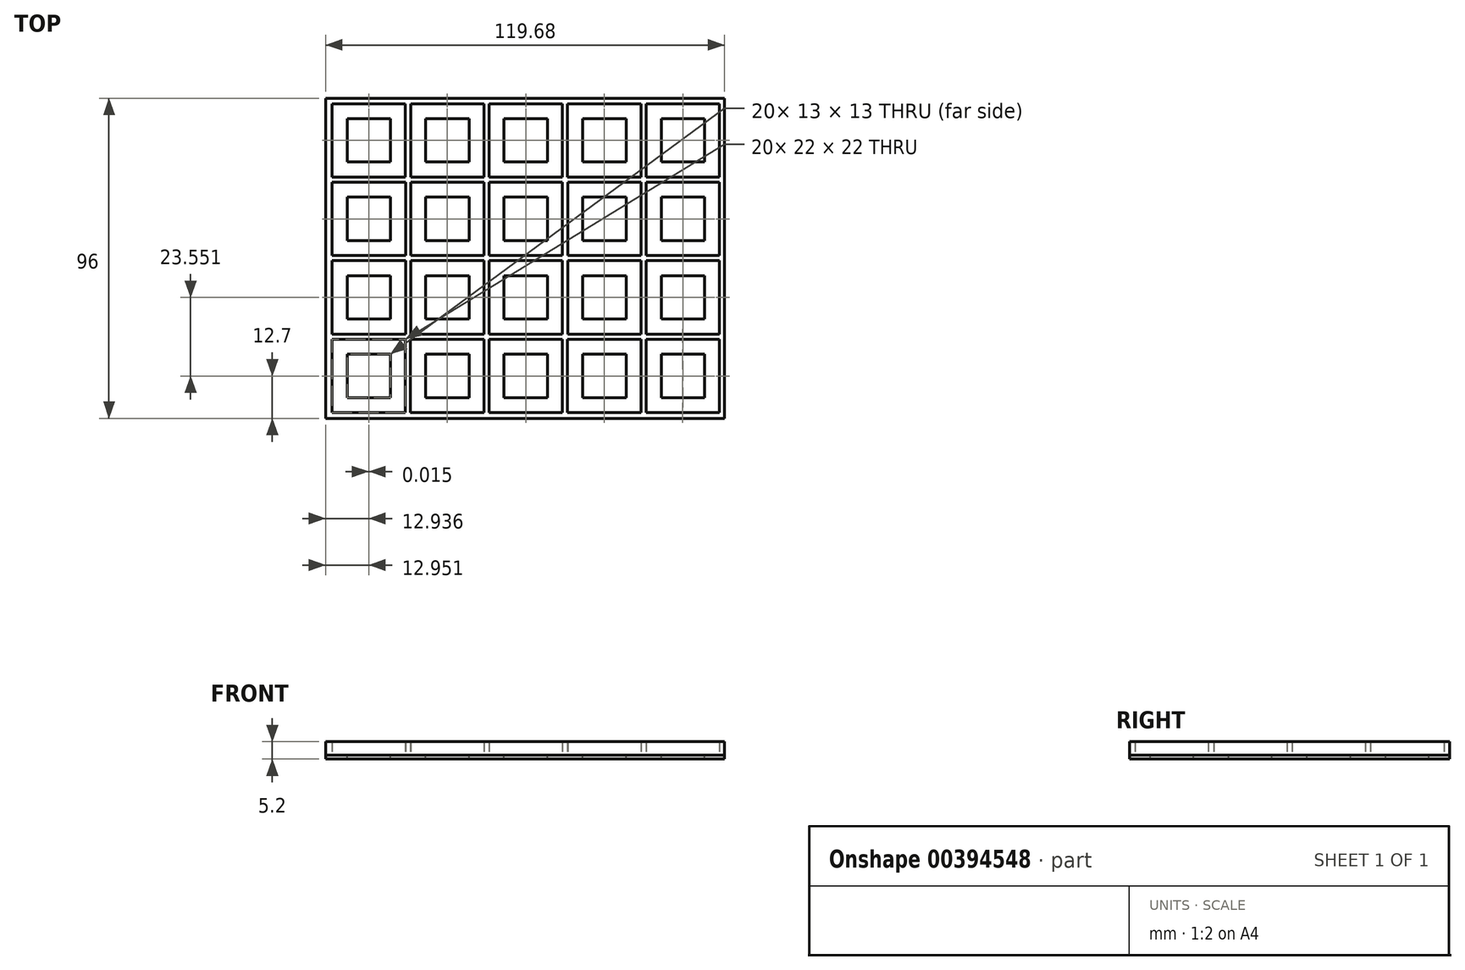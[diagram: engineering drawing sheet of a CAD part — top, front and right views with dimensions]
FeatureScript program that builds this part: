
annotation { "Feature Type Name" : "Feature", "Feature Type Description" : "" }
export const myFeature = defineFeature(function(context is Context, id is Id, definition is map)
    precondition{}
    {
        {
            var Q0;
            Q0=qCreatedBy(makeId("Top.planeOp"),FACE);
            var sketch = newSketch(context, id + "F0", { "sketchPlane" : qUnion([Q0])});
            skLineSegment(sketch, "E0", {"start": v(59.84, -48) * mm, "end": v(-59.84, -48) * mm});
            skLineSegment(sketch, "E1", {"start": v(-59.84, -48) * mm, "end": v(-59.84, 48) * mm});
            skLineSegment(sketch, "E2", {"start": v(-59.84, 48) * mm, "end": v(59.84, 48) * mm});
            skLineSegment(sketch, "E3", {"start": v(59.84, 48) * mm, "end": v(59.84, -48) * mm});
            skLineSegment(sketch, "E4", {"start": v(-35.89, 24.35) * mm, "end": v(-57.89, 24.35) * mm});
            skLineSegment(sketch, "E5", {"start": v(-57.89, 24.35) * mm, "end": v(-57.89, 46.35) * mm});
            skLineSegment(sketch, "E6", {"start": v(-57.89, 46.35) * mm, "end": v(-35.89, 46.35) * mm});
            skLineSegment(sketch, "E7", {"start": v(-35.89, 46.35) * mm, "end": v(-35.89, 24.35) * mm});
            skLineSegment(sketch, "E8", {"start": v(-35.86, 0.8) * mm, "end": v(-57.86, 0.8) * mm});
            skLineSegment(sketch, "E9", {"start": v(-57.86, 0.8) * mm, "end": v(-57.86, 22.8) * mm});
            skLineSegment(sketch, "E10", {"start": v(-57.86, 22.8) * mm, "end": v(-35.86, 22.8) * mm});
            skLineSegment(sketch, "E11", {"start": v(-35.86, 22.8) * mm, "end": v(-35.86, 0.8) * mm});
            skLineSegment(sketch, "E12", {"start": v(-35.87, -22.75) * mm, "end": v(-57.87, -22.75) * mm});
            skLineSegment(sketch, "E13", {"start": v(-57.87, -22.75) * mm, "end": v(-57.87, -0.75) * mm});
            skLineSegment(sketch, "E14", {"start": v(-57.87, -0.75) * mm, "end": v(-35.87, -0.75) * mm});
            skLineSegment(sketch, "E15", {"start": v(-35.87, -0.75) * mm, "end": v(-35.87, -22.75) * mm});
            skLineSegment(sketch, "E16", {"start": v(-35.9, -46.3) * mm, "end": v(-57.9, -46.3) * mm});
            skLineSegment(sketch, "E17", {"start": v(-57.9, -46.3) * mm, "end": v(-57.9, -24.3) * mm});
            skLineSegment(sketch, "E18", {"start": v(-57.9, -24.3) * mm, "end": v(-35.9, -24.3) * mm});
            skLineSegment(sketch, "E19", {"start": v(-35.9, -24.3) * mm, "end": v(-35.9, -46.3) * mm});
            skLineSegment(sketch, "E20", {"start": v(-12.34, 24.35) * mm, "end": v(-34.34, 24.35) * mm});
            skLineSegment(sketch, "E21", {"start": v(-34.34, 24.35) * mm, "end": v(-34.34, 46.35) * mm});
            skLineSegment(sketch, "E22", {"start": v(-34.34, 46.35) * mm, "end": v(-12.34, 46.35) * mm});
            skLineSegment(sketch, "E23", {"start": v(-12.34, 46.35) * mm, "end": v(-12.34, 24.35) * mm});
            skLineSegment(sketch, "E24", {"start": v(-12.3, 0.8) * mm, "end": v(-34.3, 0.8) * mm});
            skLineSegment(sketch, "E25", {"start": v(-34.3, 0.8) * mm, "end": v(-34.3, 22.8) * mm});
            skLineSegment(sketch, "E26", {"start": v(-34.3, 22.8) * mm, "end": v(-12.3, 22.8) * mm});
            skLineSegment(sketch, "E27", {"start": v(-12.3, 22.8) * mm, "end": v(-12.3, 0.8) * mm});
            skLineSegment(sketch, "E28", {"start": v(-12.32, -22.75) * mm, "end": v(-34.32, -22.75) * mm});
            skLineSegment(sketch, "E29", {"start": v(-34.32, -22.75) * mm, "end": v(-34.32, -0.75) * mm});
            skLineSegment(sketch, "E30", {"start": v(-34.32, -0.75) * mm, "end": v(-12.32, -0.75) * mm});
            skLineSegment(sketch, "E31", {"start": v(-12.32, -0.75) * mm, "end": v(-12.32, -22.75) * mm});
            skLineSegment(sketch, "E32", {"start": v(-12.35, -46.3) * mm, "end": v(-34.35, -46.3) * mm});
            skLineSegment(sketch, "E33", {"start": v(-34.35, -46.3) * mm, "end": v(-34.35, -24.3) * mm});
            skLineSegment(sketch, "E34", {"start": v(-34.35, -24.3) * mm, "end": v(-12.35, -24.3) * mm});
            skLineSegment(sketch, "E35", {"start": v(-12.35, -24.3) * mm, "end": v(-12.35, -46.3) * mm});
            skLineSegment(sketch, "E36", {"start": v(11.21, 24.35) * mm, "end": v(-10.79, 24.35) * mm});
            skLineSegment(sketch, "E37", {"start": v(-10.79, 24.35) * mm, "end": v(-10.79, 46.35) * mm});
            skLineSegment(sketch, "E38", {"start": v(-10.79, 46.35) * mm, "end": v(11.21, 46.35) * mm});
            skLineSegment(sketch, "E39", {"start": v(11.21, 46.35) * mm, "end": v(11.21, 24.35) * mm});
            skLineSegment(sketch, "E40", {"start": v(11.24, 0.8) * mm, "end": v(-10.76, 0.8) * mm});
            skLineSegment(sketch, "E41", {"start": v(-10.76, 0.8) * mm, "end": v(-10.76, 22.8) * mm});
            skLineSegment(sketch, "E42", {"start": v(-10.76, 22.8) * mm, "end": v(11.24, 22.8) * mm});
            skLineSegment(sketch, "E43", {"start": v(11.24, 22.8) * mm, "end": v(11.24, 0.8) * mm});
            skLineSegment(sketch, "E44", {"start": v(11.23, -22.75) * mm, "end": v(-10.77, -22.75) * mm});
            skLineSegment(sketch, "E45", {"start": v(-10.77, -22.75) * mm, "end": v(-10.77, -0.75) * mm});
            skLineSegment(sketch, "E46", {"start": v(-10.77, -0.75) * mm, "end": v(11.23, -0.75) * mm});
            skLineSegment(sketch, "E47", {"start": v(11.23, -0.75) * mm, "end": v(11.23, -22.75) * mm});
            skLineSegment(sketch, "E48", {"start": v(11.2, -46.3) * mm, "end": v(-10.8, -46.3) * mm});
            skLineSegment(sketch, "E49", {"start": v(-10.8, -46.3) * mm, "end": v(-10.8, -24.3) * mm});
            skLineSegment(sketch, "E50", {"start": v(-10.8, -24.3) * mm, "end": v(11.2, -24.3) * mm});
            skLineSegment(sketch, "E51", {"start": v(11.2, -24.3) * mm, "end": v(11.2, -46.3) * mm});
            skLineSegment(sketch, "E52", {"start": v(34.76, 24.35) * mm, "end": v(12.76, 24.35) * mm});
            skLineSegment(sketch, "E53", {"start": v(12.76, 24.35) * mm, "end": v(12.76, 46.35) * mm});
            skLineSegment(sketch, "E54", {"start": v(12.76, 46.35) * mm, "end": v(34.76, 46.35) * mm});
            skLineSegment(sketch, "E55", {"start": v(34.76, 46.35) * mm, "end": v(34.76, 24.35) * mm});
            skLineSegment(sketch, "E56", {"start": v(34.8, 0.8) * mm, "end": v(12.8, 0.8) * mm});
            skLineSegment(sketch, "E57", {"start": v(12.8, 0.8) * mm, "end": v(12.8, 22.8) * mm});
            skLineSegment(sketch, "E58", {"start": v(12.8, 22.8) * mm, "end": v(34.8, 22.8) * mm});
            skLineSegment(sketch, "E59", {"start": v(34.8, 22.8) * mm, "end": v(34.8, 0.8) * mm});
            skLineSegment(sketch, "E60", {"start": v(34.78, -22.75) * mm, "end": v(12.78, -22.75) * mm});
            skLineSegment(sketch, "E61", {"start": v(12.78, -22.75) * mm, "end": v(12.78, -0.75) * mm});
            skLineSegment(sketch, "E62", {"start": v(12.78, -0.75) * mm, "end": v(34.78, -0.75) * mm});
            skLineSegment(sketch, "E63", {"start": v(34.78, -0.75) * mm, "end": v(34.78, -22.75) * mm});
            skLineSegment(sketch, "E64", {"start": v(34.75, -46.3) * mm, "end": v(12.75, -46.3) * mm});
            skLineSegment(sketch, "E65", {"start": v(12.75, -46.3) * mm, "end": v(12.75, -24.3) * mm});
            skLineSegment(sketch, "E66", {"start": v(12.75, -24.3) * mm, "end": v(34.75, -24.3) * mm});
            skLineSegment(sketch, "E67", {"start": v(34.75, -24.3) * mm, "end": v(34.75, -46.3) * mm});
            skLineSegment(sketch, "E68", {"start": v(58.31, 24.35) * mm, "end": v(36.31, 24.35) * mm});
            skLineSegment(sketch, "E69", {"start": v(36.31, 24.35) * mm, "end": v(36.31, 46.35) * mm});
            skLineSegment(sketch, "E70", {"start": v(36.31, 46.35) * mm, "end": v(58.31, 46.35) * mm});
            skLineSegment(sketch, "E71", {"start": v(58.31, 46.35) * mm, "end": v(58.31, 24.35) * mm});
            skLineSegment(sketch, "E72", {"start": v(58.34, 0.8) * mm, "end": v(36.34, 0.8) * mm});
            skLineSegment(sketch, "E73", {"start": v(36.34, 0.8) * mm, "end": v(36.34, 22.8) * mm});
            skLineSegment(sketch, "E74", {"start": v(36.34, 22.8) * mm, "end": v(58.34, 22.8) * mm});
            skLineSegment(sketch, "E75", {"start": v(58.34, 22.8) * mm, "end": v(58.34, 0.8) * mm});
            skLineSegment(sketch, "E76", {"start": v(58.33, -22.75) * mm, "end": v(36.33, -22.75) * mm});
            skLineSegment(sketch, "E77", {"start": v(36.33, -22.75) * mm, "end": v(36.33, -0.75) * mm});
            skLineSegment(sketch, "E78", {"start": v(36.33, -0.75) * mm, "end": v(58.33, -0.75) * mm});
            skLineSegment(sketch, "E79", {"start": v(58.33, -0.75) * mm, "end": v(58.33, -22.75) * mm});
            skLineSegment(sketch, "E80", {"start": v(58.3, -46.3) * mm, "end": v(36.3, -46.3) * mm});
            skLineSegment(sketch, "E81", {"start": v(36.3, -46.3) * mm, "end": v(36.3, -24.3) * mm});
            skLineSegment(sketch, "E82", {"start": v(36.3, -24.3) * mm, "end": v(58.3, -24.3) * mm});
            skLineSegment(sketch, "E83", {"start": v(58.3, -24.3) * mm, "end": v(58.3, -46.3) * mm});
            skLineSegment(sketch, "E84", {"start": v(-40.39, 28.85) * mm, "end": v(-53.39, 28.85) * mm});
            skLineSegment(sketch, "E85", {"start": v(-53.39, 28.85) * mm, "end": v(-53.39, 41.85) * mm});
            skLineSegment(sketch, "E86", {"start": v(-53.39, 41.85) * mm, "end": v(-40.39, 41.85) * mm});
            skLineSegment(sketch, "E87", {"start": v(-40.39, 41.85) * mm, "end": v(-40.39, 28.85) * mm});
            skLineSegment(sketch, "E88", {"start": v(-16.8, 28.85) * mm, "end": v(-29.8, 28.85) * mm});
            skLineSegment(sketch, "E89", {"start": v(-29.8, 28.85) * mm, "end": v(-29.8, 41.85) * mm});
            skLineSegment(sketch, "E90", {"start": v(-29.8, 41.85) * mm, "end": v(-16.8, 41.85) * mm});
            skLineSegment(sketch, "E91", {"start": v(-16.8, 41.85) * mm, "end": v(-16.8, 28.85) * mm});
            skLineSegment(sketch, "E92", {"start": v(6.7, 28.85) * mm, "end": v(-6.3, 28.85) * mm});
            skLineSegment(sketch, "E93", {"start": v(-6.3, 28.85) * mm, "end": v(-6.3, 41.85) * mm});
            skLineSegment(sketch, "E94", {"start": v(-6.3, 41.85) * mm, "end": v(6.7, 41.85) * mm});
            skLineSegment(sketch, "E95", {"start": v(6.7, 41.85) * mm, "end": v(6.7, 28.85) * mm});
            skLineSegment(sketch, "E96", {"start": v(30.3, 28.85) * mm, "end": v(17.3, 28.85) * mm});
            skLineSegment(sketch, "E97", {"start": v(17.3, 28.85) * mm, "end": v(17.3, 41.85) * mm});
            skLineSegment(sketch, "E98", {"start": v(17.3, 41.85) * mm, "end": v(30.3, 41.85) * mm});
            skLineSegment(sketch, "E99", {"start": v(30.3, 41.85) * mm, "end": v(30.3, 28.85) * mm});
            skLineSegment(sketch, "E100", {"start": v(53.84, 28.85) * mm, "end": v(40.84, 28.85) * mm});
            skLineSegment(sketch, "E101", {"start": v(40.84, 28.85) * mm, "end": v(40.84, 41.85) * mm});
            skLineSegment(sketch, "E102", {"start": v(40.84, 41.85) * mm, "end": v(53.84, 41.85) * mm});
            skLineSegment(sketch, "E103", {"start": v(53.84, 41.85) * mm, "end": v(53.84, 28.85) * mm});
            skLineSegment(sketch, "E104", {"start": v(-40.39, 5.3) * mm, "end": v(-53.39, 5.3) * mm});
            skLineSegment(sketch, "E105", {"start": v(-53.39, 5.3) * mm, "end": v(-53.39, 18.3) * mm});
            skLineSegment(sketch, "E106", {"start": v(-53.39, 18.3) * mm, "end": v(-40.39, 18.3) * mm});
            skLineSegment(sketch, "E107", {"start": v(-40.39, 18.3) * mm, "end": v(-40.39, 5.3) * mm});
            skLineSegment(sketch, "E108", {"start": v(-16.8, 5.3) * mm, "end": v(-29.8, 5.3) * mm});
            skLineSegment(sketch, "E109", {"start": v(-29.8, 5.3) * mm, "end": v(-29.8, 18.3) * mm});
            skLineSegment(sketch, "E110", {"start": v(-29.8, 18.3) * mm, "end": v(-16.8, 18.3) * mm});
            skLineSegment(sketch, "E111", {"start": v(-16.8, 18.3) * mm, "end": v(-16.8, 5.3) * mm});
            skLineSegment(sketch, "E112", {"start": v(6.7, 5.3) * mm, "end": v(-6.3, 5.3) * mm});
            skLineSegment(sketch, "E113", {"start": v(-6.3, 5.3) * mm, "end": v(-6.3, 18.3) * mm});
            skLineSegment(sketch, "E114", {"start": v(-6.3, 18.3) * mm, "end": v(6.7, 18.3) * mm});
            skLineSegment(sketch, "E115", {"start": v(6.7, 18.3) * mm, "end": v(6.7, 5.3) * mm});
            skLineSegment(sketch, "E116", {"start": v(30.3, 5.3) * mm, "end": v(17.3, 5.3) * mm});
            skLineSegment(sketch, "E117", {"start": v(17.3, 5.3) * mm, "end": v(17.3, 18.3) * mm});
            skLineSegment(sketch, "E118", {"start": v(17.3, 18.3) * mm, "end": v(30.3, 18.3) * mm});
            skLineSegment(sketch, "E119", {"start": v(30.3, 18.3) * mm, "end": v(30.3, 5.3) * mm});
            skLineSegment(sketch, "E120", {"start": v(53.84, 5.3) * mm, "end": v(40.84, 5.3) * mm});
            skLineSegment(sketch, "E121", {"start": v(40.84, 5.3) * mm, "end": v(40.84, 18.3) * mm});
            skLineSegment(sketch, "E122", {"start": v(40.84, 18.3) * mm, "end": v(53.84, 18.3) * mm});
            skLineSegment(sketch, "E123", {"start": v(53.84, 18.3) * mm, "end": v(53.84, 5.3) * mm});
            skLineSegment(sketch, "E124", {"start": v(-40.39, -18.25) * mm, "end": v(-53.39, -18.25) * mm});
            skLineSegment(sketch, "E125", {"start": v(-53.39, -18.25) * mm, "end": v(-53.39, -5.25) * mm});
            skLineSegment(sketch, "E126", {"start": v(-53.39, -5.25) * mm, "end": v(-40.39, -5.25) * mm});
            skLineSegment(sketch, "E127", {"start": v(-40.39, -5.25) * mm, "end": v(-40.39, -18.25) * mm});
            skLineSegment(sketch, "E128", {"start": v(-16.8, -18.25) * mm, "end": v(-29.8, -18.25) * mm});
            skLineSegment(sketch, "E129", {"start": v(-29.8, -18.25) * mm, "end": v(-29.8, -5.25) * mm});
            skLineSegment(sketch, "E130", {"start": v(-29.8, -5.25) * mm, "end": v(-16.8, -5.25) * mm});
            skLineSegment(sketch, "E131", {"start": v(-16.8, -5.25) * mm, "end": v(-16.8, -18.25) * mm});
            skLineSegment(sketch, "E132", {"start": v(6.7, -18.25) * mm, "end": v(-6.3, -18.25) * mm});
            skLineSegment(sketch, "E133", {"start": v(-6.3, -18.25) * mm, "end": v(-6.3, -5.25) * mm});
            skLineSegment(sketch, "E134", {"start": v(-6.3, -5.25) * mm, "end": v(6.7, -5.25) * mm});
            skLineSegment(sketch, "E135", {"start": v(6.7, -5.25) * mm, "end": v(6.7, -18.25) * mm});
            skLineSegment(sketch, "E136", {"start": v(30.3, -18.25) * mm, "end": v(17.3, -18.25) * mm});
            skLineSegment(sketch, "E137", {"start": v(17.3, -18.25) * mm, "end": v(17.3, -5.25) * mm});
            skLineSegment(sketch, "E138", {"start": v(17.3, -5.25) * mm, "end": v(30.3, -5.25) * mm});
            skLineSegment(sketch, "E139", {"start": v(30.3, -5.25) * mm, "end": v(30.3, -18.25) * mm});
            skLineSegment(sketch, "E140", {"start": v(53.84, -18.25) * mm, "end": v(40.84, -18.25) * mm});
            skLineSegment(sketch, "E141", {"start": v(40.84, -18.25) * mm, "end": v(40.84, -5.25) * mm});
            skLineSegment(sketch, "E142", {"start": v(40.84, -5.25) * mm, "end": v(53.84, -5.25) * mm});
            skLineSegment(sketch, "E143", {"start": v(53.84, -5.25) * mm, "end": v(53.84, -18.25) * mm});
            skLineSegment(sketch, "E144", {"start": v(-40.39, -41.8) * mm, "end": v(-53.39, -41.8) * mm});
            skLineSegment(sketch, "E145", {"start": v(-53.39, -41.8) * mm, "end": v(-53.39, -28.8) * mm});
            skLineSegment(sketch, "E146", {"start": v(-53.39, -28.8) * mm, "end": v(-40.39, -28.8) * mm});
            skLineSegment(sketch, "E147", {"start": v(-40.39, -28.8) * mm, "end": v(-40.39, -41.8) * mm});
            skLineSegment(sketch, "E148", {"start": v(-16.8, -41.8) * mm, "end": v(-29.8, -41.8) * mm});
            skLineSegment(sketch, "E149", {"start": v(-29.8, -41.8) * mm, "end": v(-29.8, -28.8) * mm});
            skLineSegment(sketch, "E150", {"start": v(-29.8, -28.8) * mm, "end": v(-16.8, -28.8) * mm});
            skLineSegment(sketch, "E151", {"start": v(-16.8, -28.8) * mm, "end": v(-16.8, -41.8) * mm});
            skLineSegment(sketch, "E152", {"start": v(6.7, -41.8) * mm, "end": v(-6.3, -41.8) * mm});
            skLineSegment(sketch, "E153", {"start": v(-6.3, -41.8) * mm, "end": v(-6.3, -28.8) * mm});
            skLineSegment(sketch, "E154", {"start": v(-6.3, -28.8) * mm, "end": v(6.7, -28.8) * mm});
            skLineSegment(sketch, "E155", {"start": v(6.7, -28.8) * mm, "end": v(6.7, -41.8) * mm});
            skLineSegment(sketch, "E156", {"start": v(30.3, -41.8) * mm, "end": v(17.3, -41.8) * mm});
            skLineSegment(sketch, "E157", {"start": v(17.3, -41.8) * mm, "end": v(17.3, -28.8) * mm});
            skLineSegment(sketch, "E158", {"start": v(17.3, -28.8) * mm, "end": v(30.3, -28.8) * mm});
            skLineSegment(sketch, "E159", {"start": v(30.3, -28.8) * mm, "end": v(30.3, -41.8) * mm});
            skLineSegment(sketch, "E160", {"start": v(53.84, -41.8) * mm, "end": v(40.84, -41.8) * mm});
            skLineSegment(sketch, "E161", {"start": v(40.84, -41.8) * mm, "end": v(40.84, -28.8) * mm});
            skLineSegment(sketch, "E162", {"start": v(40.84, -28.8) * mm, "end": v(53.84, -28.8) * mm});
            skLineSegment(sketch, "E163", {"start": v(53.84, -28.8) * mm, "end": v(53.84, -41.8) * mm});
            skSolve(sketch);
        }
        {
            var Q0;
            Q0=makeQuery(id+"F0.imprint","IMPRINT",FACE,{"disambiguationData":[TD([[makeQuery(id+"F0.imprint","IMPRINT",EDGE,{"derivedFrom":sQuery(id+"F0.wireOp",EDGE,"E0")}),-1.0]])]});
            extrude(context, id + "F1", {"entities" : qUnion([Q0]), "depth" : 4 * mm});
        }
        {
            var Q0;
            Q0=makeQuery(id+"F0.imprint","IMPRINT",FACE,{"disambiguationData":[TD([[makeQuery(id+"F0.imprint","IMPRINT",EDGE,{"derivedFrom":sQuery(id+"F0.wireOp",EDGE,"E64")}),-1.0]])]});
            var Q1;
            Q1=makeQuery(id+"F0.imprint","IMPRINT",FACE,{"disambiguationData":[TD([[makeQuery(id+"F0.imprint","IMPRINT",EDGE,{"derivedFrom":sQuery(id+"F0.wireOp",EDGE,"E28")}),-1.0]])]});
            var Q2;
            Q2=makeQuery(id+"F0.imprint","IMPRINT",FACE,{"disambiguationData":[TD([[makeQuery(id+"F0.imprint","IMPRINT",EDGE,{"derivedFrom":sQuery(id+"F0.wireOp",EDGE,"E4")}),-1.0]])]});
            var Q3;
            Q3=makeQuery(id+"F0.imprint","IMPRINT",FACE,{"disambiguationData":[TD([[makeQuery(id+"F0.imprint","IMPRINT",EDGE,{"derivedFrom":sQuery(id+"F0.wireOp",EDGE,"E68")}),-1.0]])]});
            var Q4;
            Q4=makeQuery(id+"F0.imprint","IMPRINT",FACE,{"disambiguationData":[TD([[makeQuery(id+"F0.imprint","IMPRINT",EDGE,{"derivedFrom":sQuery(id+"F0.wireOp",EDGE,"E40")}),-1.0]])]});
            var Q5;
            Q5=makeQuery(id+"F0.imprint","IMPRINT",FACE,{"disambiguationData":[TD([[makeQuery(id+"F0.imprint","IMPRINT",EDGE,{"derivedFrom":sQuery(id+"F0.wireOp",EDGE,"E32")}),-1.0]])]});
            var Q6;
            Q6=makeQuery(id+"F0.imprint","IMPRINT",FACE,{"disambiguationData":[TD([[makeQuery(id+"F0.imprint","IMPRINT",EDGE,{"derivedFrom":sQuery(id+"F0.wireOp",EDGE,"E8")}),-1.0]])]});
            var Q7;
            Q7=makeQuery(id+"F0.imprint","IMPRINT",FACE,{"disambiguationData":[TD([[makeQuery(id+"F0.imprint","IMPRINT",EDGE,{"derivedFrom":sQuery(id+"F0.wireOp",EDGE,"E44")}),-1.0]])]});
            var Q8;
            Q8=makeQuery(id+"F0.imprint","IMPRINT",FACE,{"disambiguationData":[TD([[makeQuery(id+"F0.imprint","IMPRINT",EDGE,{"derivedFrom":sQuery(id+"F0.wireOp",EDGE,"E72")}),-1.0]])]});
            var Q9;
            Q9=makeQuery(id+"F0.imprint","IMPRINT",FACE,{"disambiguationData":[TD([[makeQuery(id+"F0.imprint","IMPRINT",EDGE,{"derivedFrom":sQuery(id+"F0.wireOp",EDGE,"E36")}),-1.0]])]});
            var Q10;
            Q10=makeQuery(id+"F0.imprint","IMPRINT",FACE,{"disambiguationData":[TD([[makeQuery(id+"F0.imprint","IMPRINT",EDGE,{"derivedFrom":sQuery(id+"F0.wireOp",EDGE,"E76")}),-1.0]])]});
            var Q11;
            Q11=makeQuery(id+"F0.imprint","IMPRINT",FACE,{"disambiguationData":[TD([[makeQuery(id+"F0.imprint","IMPRINT",EDGE,{"derivedFrom":sQuery(id+"F0.wireOp",EDGE,"E12")}),-1.0]])]});
            var Q12;
            Q12=makeQuery(id+"F0.imprint","IMPRINT",FACE,{"disambiguationData":[TD([[makeQuery(id+"F0.imprint","IMPRINT",EDGE,{"derivedFrom":sQuery(id+"F0.wireOp",EDGE,"E52")}),-1.0]])]});
            var Q13;
            Q13=makeQuery(id+"F0.imprint","IMPRINT",FACE,{"disambiguationData":[TD([[makeQuery(id+"F0.imprint","IMPRINT",EDGE,{"derivedFrom":sQuery(id+"F0.wireOp",EDGE,"E80")}),-1.0]])]});
            var Q14;
            Q14=makeQuery(id+"F0.imprint","IMPRINT",FACE,{"disambiguationData":[TD([[makeQuery(id+"F0.imprint","IMPRINT",EDGE,{"derivedFrom":sQuery(id+"F0.wireOp",EDGE,"E16")}),-1.0]])]});
            var Q15;
            Q15=makeQuery(id+"F0.imprint","IMPRINT",FACE,{"disambiguationData":[TD([[makeQuery(id+"F0.imprint","IMPRINT",EDGE,{"derivedFrom":sQuery(id+"F0.wireOp",EDGE,"E56")}),-1.0]])]});
            var Q16;
            Q16=makeQuery(id+"F0.imprint","IMPRINT",FACE,{"disambiguationData":[TD([[makeQuery(id+"F0.imprint","IMPRINT",EDGE,{"derivedFrom":sQuery(id+"F0.wireOp",EDGE,"E0")}),-1.0]])]});
            var Q17;
            Q17=makeQuery(id+"F0.imprint","IMPRINT",FACE,{"disambiguationData":[TD([[makeQuery(id+"F0.imprint","IMPRINT",EDGE,{"derivedFrom":sQuery(id+"F0.wireOp",EDGE,"E20")}),-1.0]])]});
            var Q18;
            Q18=makeQuery(id+"F0.imprint","IMPRINT",FACE,{"disambiguationData":[TD([[makeQuery(id+"F0.imprint","IMPRINT",EDGE,{"derivedFrom":sQuery(id+"F0.wireOp",EDGE,"E60")}),-1.0]])]});
            var Q19;
            Q19=makeQuery(id+"F0.imprint","IMPRINT",FACE,{"disambiguationData":[TD([[makeQuery(id+"F0.imprint","IMPRINT",EDGE,{"derivedFrom":sQuery(id+"F0.wireOp",EDGE,"E48")}),-1.0]])]});
            var Q20;
            Q20=makeQuery(id+"F0.imprint","IMPRINT",FACE,{"disambiguationData":[TD([[makeQuery(id+"F0.imprint","IMPRINT",EDGE,{"derivedFrom":sQuery(id+"F0.wireOp",EDGE,"E24")}),-1.0]])]});
            extrude(context, id + "F2", {"entities" : qUnion([Q0, Q1, Q2, Q3, Q4, Q5, Q6, Q7, Q8, Q9, Q10, Q11, Q12, Q13, Q14, Q15, Q16, Q17, Q18, Q19, Q20]), "oppositeDirection" : true, "depth" : 1.2 * mm});
        }
    });
